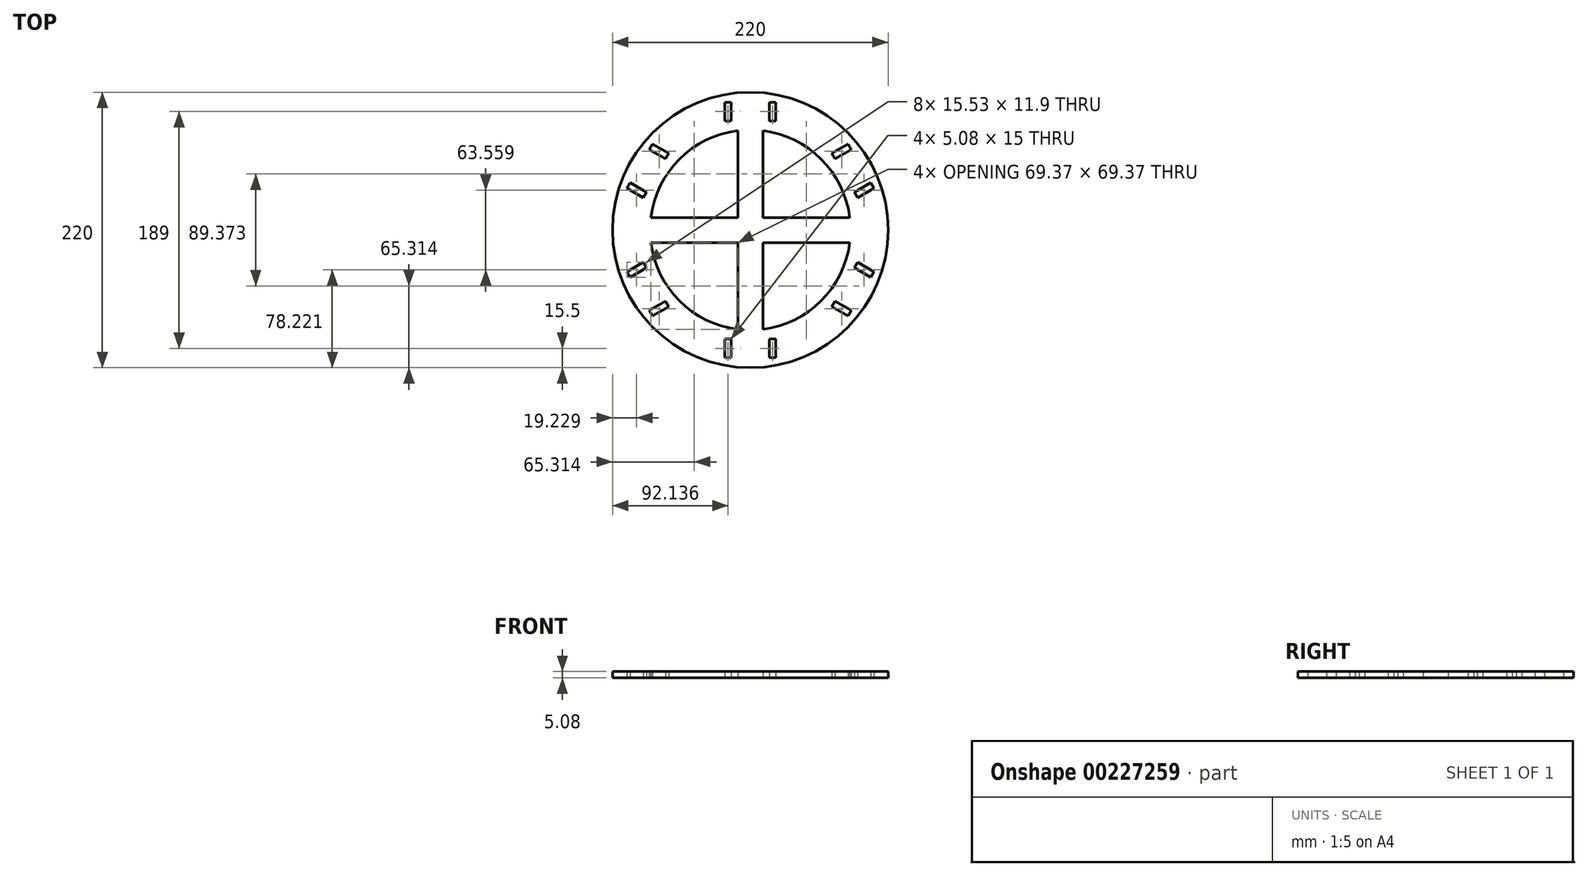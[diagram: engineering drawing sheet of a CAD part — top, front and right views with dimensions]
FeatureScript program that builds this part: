
annotation { "Feature Type Name" : "Feature", "Feature Type Description" : "" }
export const myFeature = defineFeature(function(context is Context, id is Id, definition is map)
    precondition{}
    {
        {
            var Q0;
            Q0=qCreatedBy(makeId("Top.planeOp"),FACE);
            var sketch = newSketch(context, id + "F0", { "sketchPlane" : qUnion([Q0])});
            skCircle(sketch, "E0", {"center": v(0, 0) * mm, "radius": 110 * mm});
            skArc(sketch, "E1", {"start": v(-10, 79.37) * mm, "mid": v(-56.57, 56.57) * mm, "end": v(-79.37, 10) * mm});
            skLineSegment(sketch, "E2.bottom", {"start": v(-20.4, 102) * mm, "end": v(-15.32, 102) * mm});
            skLineSegment(sketch, "E2.top", {"start": v(-20.4, 87) * mm, "end": v(-15.32, 87) * mm});
            skLineSegment(sketch, "E2.left", {"start": v(-20.4, 102) * mm, "end": v(-20.4, 87) * mm});
            skLineSegment(sketch, "E2.right", {"start": v(-15.32, 102) * mm, "end": v(-15.32, 87) * mm});
            skLineSegment(sketch, "E3", {"start": v(0, 0) * mm, "end": v(0, 117.32) * mm, "construction": true});
            skLineSegment(sketch, "E4.MirrorCS", {"start": v(15.32, 102) * mm, "end": v(15.32, 87) * mm});
            skLineSegment(sketch, "E5.MirrorCS", {"start": v(20.4, 102) * mm, "end": v(15.32, 102) * mm});
            skLineSegment(sketch, "E6.MirrorCS", {"start": v(20.4, 102) * mm, "end": v(20.4, 87) * mm});
            skLineSegment(sketch, "E7.MirrorCS", {"start": v(20.4, 87) * mm, "end": v(15.32, 87) * mm});
            skLineSegment(sketch, "E8.1.0", {"start": v(-98.54, 33.33) * mm, "end": v(-96, 37.73) * mm});
            skLineSegment(sketch, "E8.1.1", {"start": v(-98.54, 33.33) * mm, "end": v(-85.55, 25.83) * mm});
            skLineSegment(sketch, "E8.1.2", {"start": v(-85.55, 25.83) * mm, "end": v(-83, 30.23) * mm});
            skLineSegment(sketch, "E8.1.3", {"start": v(-96, 37.73) * mm, "end": v(-83, 30.23) * mm});
            skLineSegment(sketch, "E8.1.4", {"start": v(-80.67, 64.27) * mm, "end": v(-67.68, 56.77) * mm});
            skLineSegment(sketch, "E8.1.5", {"start": v(-78.13, 68.67) * mm, "end": v(-80.67, 64.27) * mm});
            skLineSegment(sketch, "E8.1.6", {"start": v(-78.13, 68.67) * mm, "end": v(-65.14, 61.17) * mm});
            skLineSegment(sketch, "E8.1.7", {"start": v(-65.14, 61.17) * mm, "end": v(-67.68, 56.77) * mm});
            skLineSegment(sketch, "E8.2.0", {"start": v(-78.13, -68.67) * mm, "end": v(-80.67, -64.27) * mm});
            skLineSegment(sketch, "E8.2.1", {"start": v(-78.13, -68.67) * mm, "end": v(-65.14, -61.17) * mm});
            skLineSegment(sketch, "E8.2.2", {"start": v(-65.14, -61.17) * mm, "end": v(-67.68, -56.77) * mm});
            skLineSegment(sketch, "E8.2.3", {"start": v(-80.67, -64.27) * mm, "end": v(-67.68, -56.77) * mm});
            skLineSegment(sketch, "E8.2.4", {"start": v(-96, -37.73) * mm, "end": v(-83, -30.23) * mm});
            skLineSegment(sketch, "E8.2.5", {"start": v(-98.54, -33.33) * mm, "end": v(-96, -37.73) * mm});
            skLineSegment(sketch, "E8.2.6", {"start": v(-98.54, -33.33) * mm, "end": v(-85.55, -25.83) * mm});
            skLineSegment(sketch, "E8.2.7", {"start": v(-85.55, -25.83) * mm, "end": v(-83, -30.23) * mm});
            skLineSegment(sketch, "E8.3.0", {"start": v(20.4, -102) * mm, "end": v(15.32, -102) * mm});
            skLineSegment(sketch, "E8.3.1", {"start": v(20.4, -102) * mm, "end": v(20.4, -87) * mm});
            skLineSegment(sketch, "E8.3.2", {"start": v(20.4, -87) * mm, "end": v(15.32, -87) * mm});
            skLineSegment(sketch, "E8.3.3", {"start": v(15.32, -102) * mm, "end": v(15.32, -87) * mm});
            skLineSegment(sketch, "E8.3.4", {"start": v(-15.32, -102) * mm, "end": v(-15.32, -87) * mm});
            skLineSegment(sketch, "E8.3.5", {"start": v(-20.4, -102) * mm, "end": v(-15.32, -102) * mm});
            skLineSegment(sketch, "E8.3.6", {"start": v(-20.4, -102) * mm, "end": v(-20.4, -87) * mm});
            skLineSegment(sketch, "E8.3.7", {"start": v(-20.4, -87) * mm, "end": v(-15.32, -87) * mm});
            skLineSegment(sketch, "E8.4.0", {"start": v(98.54, -33.33) * mm, "end": v(96, -37.73) * mm});
            skLineSegment(sketch, "E8.4.1", {"start": v(98.54, -33.33) * mm, "end": v(85.55, -25.83) * mm});
            skLineSegment(sketch, "E8.4.2", {"start": v(85.55, -25.83) * mm, "end": v(83, -30.23) * mm});
            skLineSegment(sketch, "E8.4.3", {"start": v(96, -37.73) * mm, "end": v(83, -30.23) * mm});
            skLineSegment(sketch, "E8.4.4", {"start": v(80.67, -64.27) * mm, "end": v(67.68, -56.77) * mm});
            skLineSegment(sketch, "E8.4.5", {"start": v(78.13, -68.67) * mm, "end": v(80.67, -64.27) * mm});
            skLineSegment(sketch, "E8.4.6", {"start": v(78.13, -68.67) * mm, "end": v(65.14, -61.17) * mm});
            skLineSegment(sketch, "E8.4.7", {"start": v(65.14, -61.17) * mm, "end": v(67.68, -56.77) * mm});
            skLineSegment(sketch, "E8.5.0", {"start": v(78.13, 68.67) * mm, "end": v(80.67, 64.27) * mm});
            skLineSegment(sketch, "E8.5.1", {"start": v(78.13, 68.67) * mm, "end": v(65.14, 61.17) * mm});
            skLineSegment(sketch, "E8.5.2", {"start": v(65.14, 61.17) * mm, "end": v(67.68, 56.77) * mm});
            skLineSegment(sketch, "E8.5.3", {"start": v(80.67, 64.27) * mm, "end": v(67.68, 56.77) * mm});
            skLineSegment(sketch, "E8.5.4", {"start": v(96, 37.73) * mm, "end": v(83, 30.23) * mm});
            skLineSegment(sketch, "E8.5.5", {"start": v(98.54, 33.33) * mm, "end": v(96, 37.73) * mm});
            skLineSegment(sketch, "E8.5.6", {"start": v(98.54, 33.33) * mm, "end": v(85.55, 25.83) * mm});
            skLineSegment(sketch, "E8.5.7", {"start": v(85.55, 25.83) * mm, "end": v(83, 30.23) * mm});
            skLineSegment(sketch, "E9", {"start": v(-10, 79.37) * mm, "end": v(-10, 10) * mm});
            skLineSegment(sketch, "E10.MirrorCS", {"start": v(10, 79.37) * mm, "end": v(10, 10) * mm});
            skArc(sketch, "E11.trimOffspring", {"start": v(10, -79.37) * mm, "mid": v(56.57, -56.57) * mm, "end": v(79.37, -10) * mm});
            skLineSegment(sketch, "E12", {"start": v(-79.37, 10) * mm, "end": v(-10, 10) * mm});
            skLineSegment(sketch, "E13.MirrorCS", {"start": v(-79.37, -10) * mm, "end": v(-10, -10) * mm});
            skLineSegment(sketch, "E14.trimOffspring", {"start": v(-10, -10) * mm, "end": v(-10, -79.37) * mm});
            skLineSegment(sketch, "E15.trimOffspring", {"start": v(10, -10) * mm, "end": v(10, -79.37) * mm});
            skArc(sketch, "E16.trimOffspring", {"start": v(-79.37, -10) * mm, "mid": v(-56.57, -56.57) * mm, "end": v(-10, -79.37) * mm});
            skArc(sketch, "E17.trimOffspring", {"start": v(79.37, 10) * mm, "mid": v(56.57, 56.57) * mm, "end": v(10, 79.37) * mm});
            skLineSegment(sketch, "E18.trimOffspring", {"start": v(10, 10) * mm, "end": v(79.37, 10) * mm});
            skLineSegment(sketch, "E19.trimOffspring", {"start": v(10, -10) * mm, "end": v(79.37, -10) * mm});
            skSolve(sketch);
        }
        {
            var Q0;
            Q0 = qSketchRegion(id + "F0", true);
            extrude(context, id + "F1", {"entities" : qUnion([Q0]), "depth" : 5.08 * mm});
        }
    });
